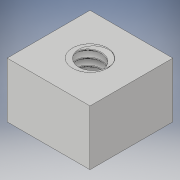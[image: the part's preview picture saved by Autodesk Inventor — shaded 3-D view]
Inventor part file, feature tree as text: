
AUTODESK INVENTOR PART (.ipt)
format: ipt  version: 2019 (Build 230136000, 136)  size: 621,568 bytes
history: native  units: in
note: dims shown in document units (in); Inventor stores cm internally (conversion verified against a paired STEP export)
features: sketch x4, extrude x2, thread x1, revolve x1, helix x1
ambient origin geometry x8: Origin, YZ Plane, XZ Plane, XY Plane, X Axis, Y Axis, Z Axis, Center Point
bodies: Solid1 (feature_tree), Solid2 (feature_tree)
feature tree (9):
  extrude  "Extrusion1"  Depth=0.5906in
  extrude  "Extrusion2"  Depth=0.3937in
  thread  "Thread1"  [1 undecoded]
  revolve  "Revolution1"  [1 undecoded]
  helix  "Coil1"  [1 undecoded]
  sketch  "Sketch1"  dims[d0=0.5906in d1=0.5906in]
  sketch  "Sketch2"  dims[d2=0.3937in d3=0.0in d4=0.25in d5=0.3937in d6=0.0in]
  sketch  "Sketch3"  dims[d7=0.3937in d8=0.0in d9=0.3779in d10=0.008in d11=0.008in d14=0.05in]
  sketch  "Sketch4"  dims[d16=0.3779in d18=0.0in d19=0.05in d20=0.4937in d21=0.3937in d22=0.0in d23=0.0in d24=0.0in d25=0.0in d26=0.0in]
note: 3 required parameter values undecoded (feature->parameter linkage not recoverable at this tier; creation-order binding heuristic only, values carry confidence <= 0.55)